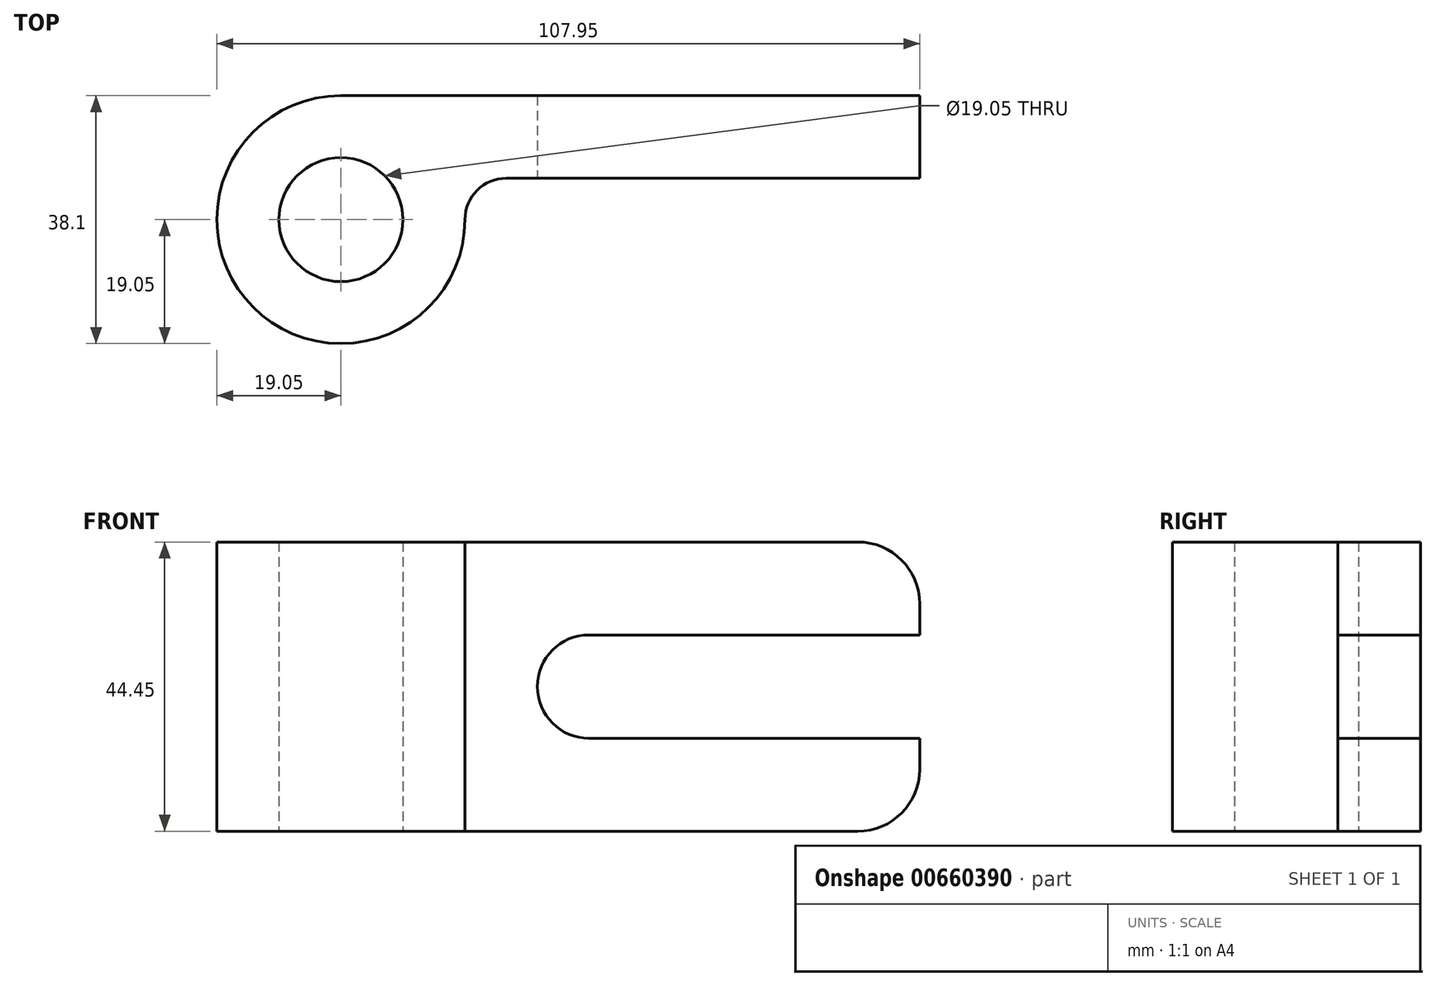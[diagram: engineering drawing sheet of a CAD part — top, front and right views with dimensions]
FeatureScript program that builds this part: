
annotation { "Feature Type Name" : "Feature", "Feature Type Description" : "" }
export const myFeature = defineFeature(function(context is Context, id is Id, definition is map)
    precondition{}
    {
        {
            var Q0;
            Q0=qCreatedBy(makeId("Top.planeOp"),FACE);
            var sketch = newSketch(context, id + "F0", { "sketchPlane" : qUnion([Q0])});
            skCircle(sketch, "E0", {"center": v(0, 0) * mm, "radius": 9.53 * mm});
            skArc(sketch, "E1", {"start": v(0, 19.05) * mm, "mid": v(-13.47, -13.47) * mm, "end": v(19.05, 0) * mm});
            skLineSegment(sketch, "E2", {"start": v(0, 19.05) * mm, "end": v(38.1, 19.05) * mm});
            skLineSegment(sketch, "E3", {"start": v(38.1, 19.05) * mm, "end": v(88.9, 19.05) * mm});
            skLineSegment(sketch, "E4", {"start": v(88.9, 19.05) * mm, "end": v(88.9, 6.35) * mm});
            skLineSegment(sketch, "E5", {"start": v(88.9, 6.35) * mm, "end": v(25.4, 6.35) * mm});
            skArc(sketch, "E6", {"start": v(25.4, 6.35) * mm, "mid": v(20.9, 4.5) * mm, "end": v(19.05, 0) * mm});
            skSolve(sketch);
        }
        {
            var Q0;
            Q0 = qSketchRegion(id + "F0", true);
            extrude(context, id + "F1", {"entities" : qUnion([Q0]), "depth" : 44.45 * mm, "offsetDistance" : 25.4 * mm});
        }
        {
            var Q0;
            Q0=makeQuery(id+"F1.opExtrude","SWEPT_FACE",FACE,{"disambiguationData":[OSD([sQuery(id+"F0.wireOp",EDGE,"E5")])]});
            var sketch = newSketch(context, id + "F2", { "sketchPlane" : qUnion([Q0])});
            skArc(sketch, "E7", {"start": v(38.1, 30.16) * mm, "mid": v(30.16, 22.22) * mm, "end": v(38.1, 14.29) * mm});
            skLineSegment(sketch, "E8", {"start": v(38.1, 14.29) * mm, "end": v(88.9, 14.29) * mm});
            skLineSegment(sketch, "E9", {"start": v(38.1, 30.16) * mm, "end": v(88.9, 30.16) * mm});
            skLineSegment(sketch, "E10", {"start": v(88.9, 0) * mm, "end": v(88.9, 44.45) * mm});
            skLineSegment(sketch, "E11", {"start": v(88.9, 44.45) * mm, "end": v(38.1, 44.45) * mm});
            skLineSegment(sketch, "E12", {"start": v(38.1, 0) * mm, "end": v(88.9, 0) * mm});
            skArc(sketch, "E13", {"start": v(88.9, 34.93) * mm, "mid": v(86.11, 41.66) * mm, "end": v(79.38, 44.45) * mm});
            skArc(sketch, "E14", {"start": v(79.38, 0) * mm, "mid": v(86.11, 2.79) * mm, "end": v(88.9, 9.53) * mm});
            skSolve(sketch);
        }
        {
            var Q0;
            {var subQ3=sQuery(id+"F2.wireOp",EDGE,"E13");Q0=makeQuery(id+"F2.imprint","IMPRINT",FACE,{"disambiguationData":[TD([[makeQuery(id+"F2.imprint","IMPRINT",EDGE,{"derivedFrom":subQ3}),-1.0]])]});}
            var Q1;
            {var subQ3=sQuery(id+"F2.wireOp",EDGE,"E14");Q1=makeQuery(id+"F2.imprint","IMPRINT",FACE,{"disambiguationData":[TD([[makeQuery(id+"F2.imprint","IMPRINT",EDGE,{"derivedFrom":subQ3}),-1.0]])]});}
            var Q2;
            Q2=makeQuery(id+"F2.imprint","IMPRINT",FACE,{"disambiguationData":[TD([[makeQuery(id+"F2.imprint","IMPRINT",EDGE,{"derivedFrom":sQuery(id+"F2.wireOp",EDGE,"E7")}),1.0]])]});
            extrude(context, id + "F3", {"entities" : qUnion([Q0, Q1, Q2]), "operationType" : NewBodyOperationType.REMOVE, "oppositeDirection" : true, "depth" : 12.7 * mm, "offsetDistance" : 25.4 * mm});
        }
    });
